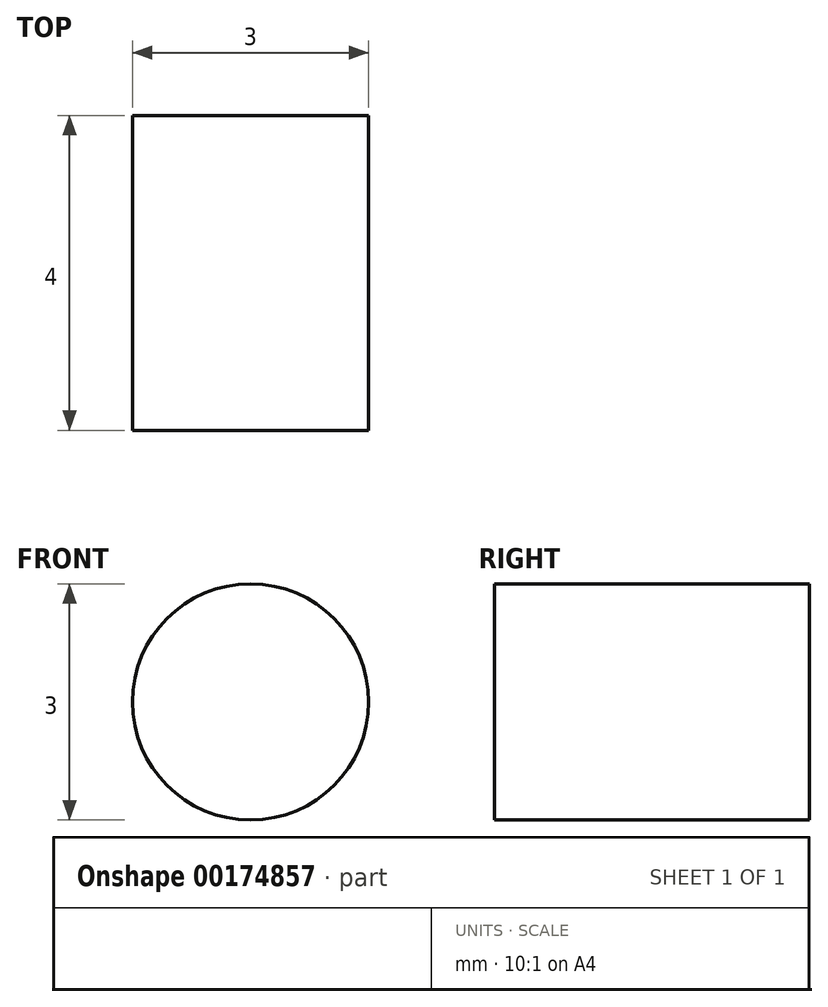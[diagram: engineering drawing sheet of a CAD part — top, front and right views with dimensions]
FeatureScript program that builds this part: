
annotation { "Feature Type Name" : "Feature", "Feature Type Description" : "" }
export const myFeature = defineFeature(function(context is Context, id is Id, definition is map)
    precondition{}
    {
        {
            var Q0;
            Q0=qCreatedBy(makeId("Front.planeOp"),FACE);
            var sketch = newSketch(context, id + "F0", { "sketchPlane" : qUnion([Q0])});
            skCircle(sketch, "E0", {"center": v(0, 0) * mm, "radius": 1.5 * mm});
            skSolve(sketch);
        }
        {
            var Q0;
            Q0 = qSketchRegion(id + "F0", true);
            extrude(context, id + "F1", {"entities" : qUnion([Q0]), "depth" : 4 * mm});
        }
    });
